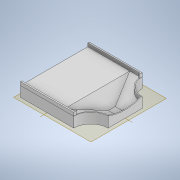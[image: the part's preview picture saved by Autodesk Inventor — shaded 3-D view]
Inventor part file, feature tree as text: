
AUTODESK INVENTOR PART (.ipt)
format: ipt  version: 2020 (Build 240168000, 168)  size: 248,832 bytes
history: native  units: mm
features: extrude x8, sketch x8, other x6, projected_geometry x2
ambient origin geometry x8: Origin, YZ Plane, XZ Plane, XY Plane, X Axis, Y Axis, Z Axis, Center Point
bodies: Body1 (feature_tree), Body2 (feature_tree), Body3 (feature_tree), Body4 (feature_tree)
feature tree (24):
  other  "Твердое тело1"
  extrude  "Выдавливание1"  Depth=200.0mm
  extrude  "Выдавливание2"  Depth=155.0mm
  extrude  "Выдавливание3"  Depth=50.0mm
  extrude  "Выдавливание4"  Depth=3.0mm TaperAngle=0.0deg
  extrude  "Выдавливание5"  Depth=27.0mm TaperAngle=0.0deg
  extrude  "Выдавливание6"  Depth=27.0mm TaperAngle=0.0deg
  extrude  "Выдавливание7"  Depth=123.5mm TaperAngle=0.0deg
  extrude  "Выдавливание8"  Depth=27.0mm TaperAngle=0.0deg
  sketch  "Эскиз1"
  sketch  "Эскиз3"
  sketch  "Эскиз4"
  other  "Твердое тело2"
  sketch  "Эскиз5"
  sketch  "Эскиз7"
  other  "Твердое тело3"
  sketch  "Эскиз8"
  projected_geometry  "Спроецированная петля3"
  projected_geometry  "Спроецированная петля4"
  sketch  "Эскиз9"
  sketch  "Эскиз10"
  other  "Твердое тело4"
  other  "Проецирование ребер5"
  other  "Проецирование ребер6"
